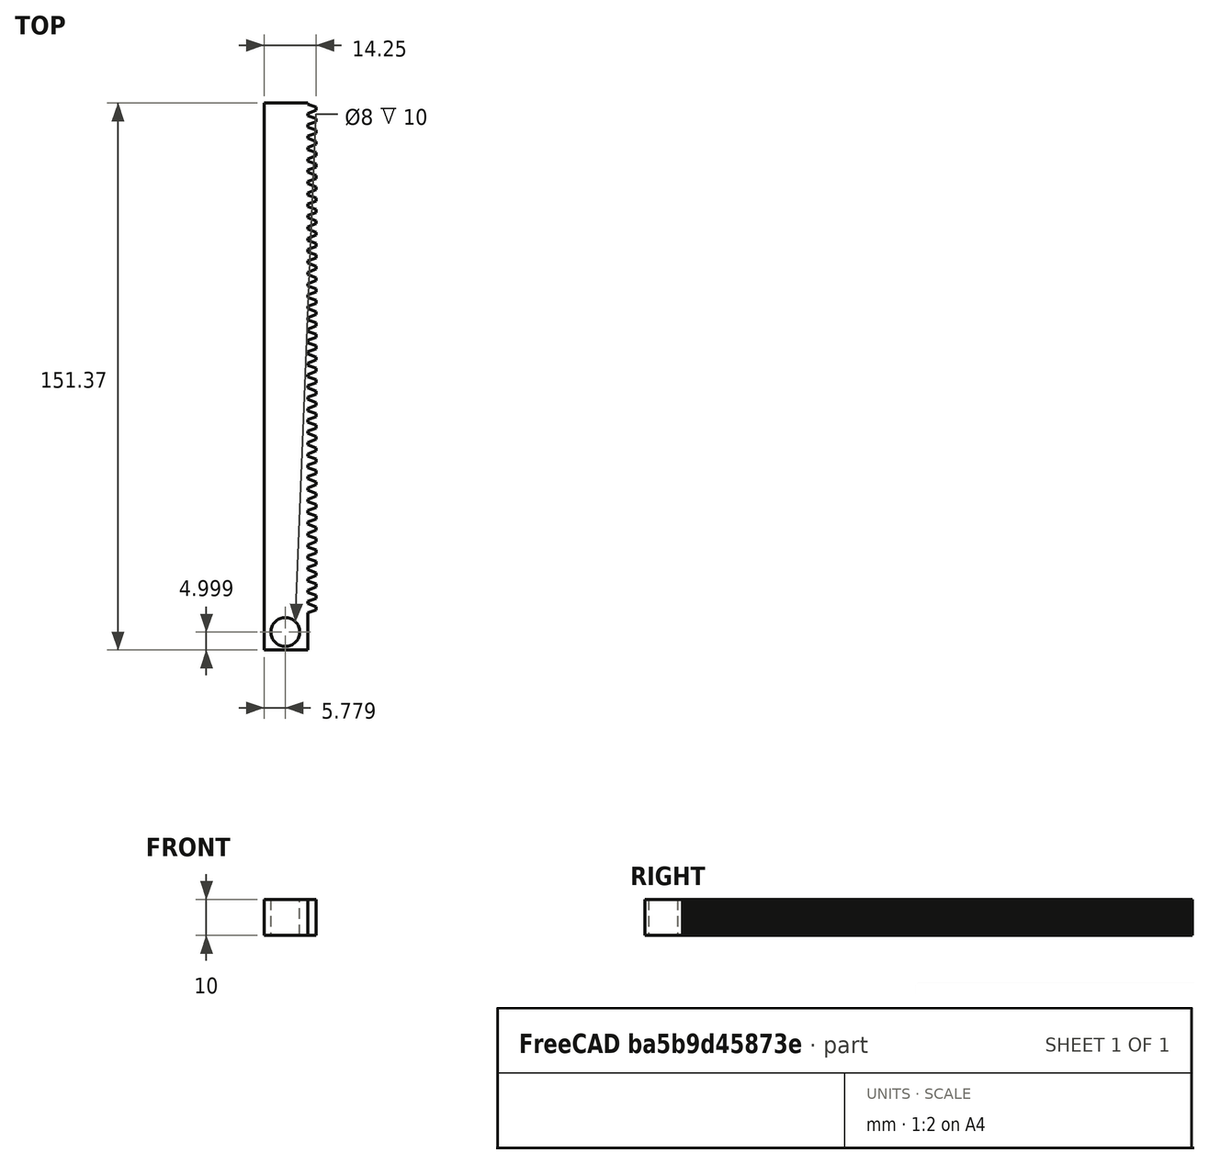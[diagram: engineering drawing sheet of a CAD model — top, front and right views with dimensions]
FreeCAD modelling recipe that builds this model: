
FCSTD DOCUMENT  (FreeCAD 0.20R29410 (Git))
Label: Rack
License: All rights reserved
LicenseURL: http://en.wikipedia.org/wiki/All_rights_reserved
objects: PartDesign::FeaturePython×1, PartDesign::Pad×1, Sketcher::SketchObject×1, PartDesign::Body×1, Part::Extrusion×1, Part::Cut×1
note: 7 computed .brp shape members not serialized (recipe doc carries the construction recipe); baked Part::Feature solids carry a one-line shape summary decoded from their .brp

FEATURE [PartDesign::FeaturePython] InvoluteRack  # WARN: FeaturePython — macro-defined, semantics opaque (R4)
  AttacherType = Attacher::AttachEngine3D
  add_endings = true
  beta = 0
  clearance = 0.25
  double_helix = false
  head = 0
  head_fillet = 0
  height = 10
  module = 1
  pressure_angle = 20
  properties_from_tool = false
  root_fillet = 0
  simplified = false
  teeth = 45
  thickness = 12
  transverse_pitch = 3.14159
  version = 0.0.4
FEATURE [PartDesign::Pad] Pad
  BaseFeature = -> InvoluteRack
  Direction = (0,-1,0)
  Length = 10
  Length2 = 10
  Profile = -> InvoluteRack [Face1]
  Type = 0
FEATURE [Sketcher::SketchObject] Sketch
  FullyConstrained = false
  MapMode = 5
  Placement = pos=(0,0,10) rot=(0,0,1;0rad)
  Support = -> [Pad]
  sketch-geometry (1):
    g0: Circle CenterX=-7.47114 CenterY=-6.5708 CenterZ=0 NormalX=0 NormalY=0 NormalZ=1 AngleXU=0 Radius=4
  constraints (1):
    c: Diameter(g0) = 8
FEATURE [PartDesign::Body] Body
  Group = -> [InvoluteRack,Pad,Sketch]
  Origin = -> Origin
  Tip = -> Pad
FEATURE [Part::Extrusion] Extrude
  Base = -> Sketch
  Dir = (0,0,1)
  DirMode = 2
  FaceMakerClass = Part::FaceMakerBullseye
  LengthFwd = 10
  LengthRev = 20
  Solid = true
  Symmetric = false
FEATURE [Part::Cut] Cut
  Base = -> Body
  Tool = -> Extrude
